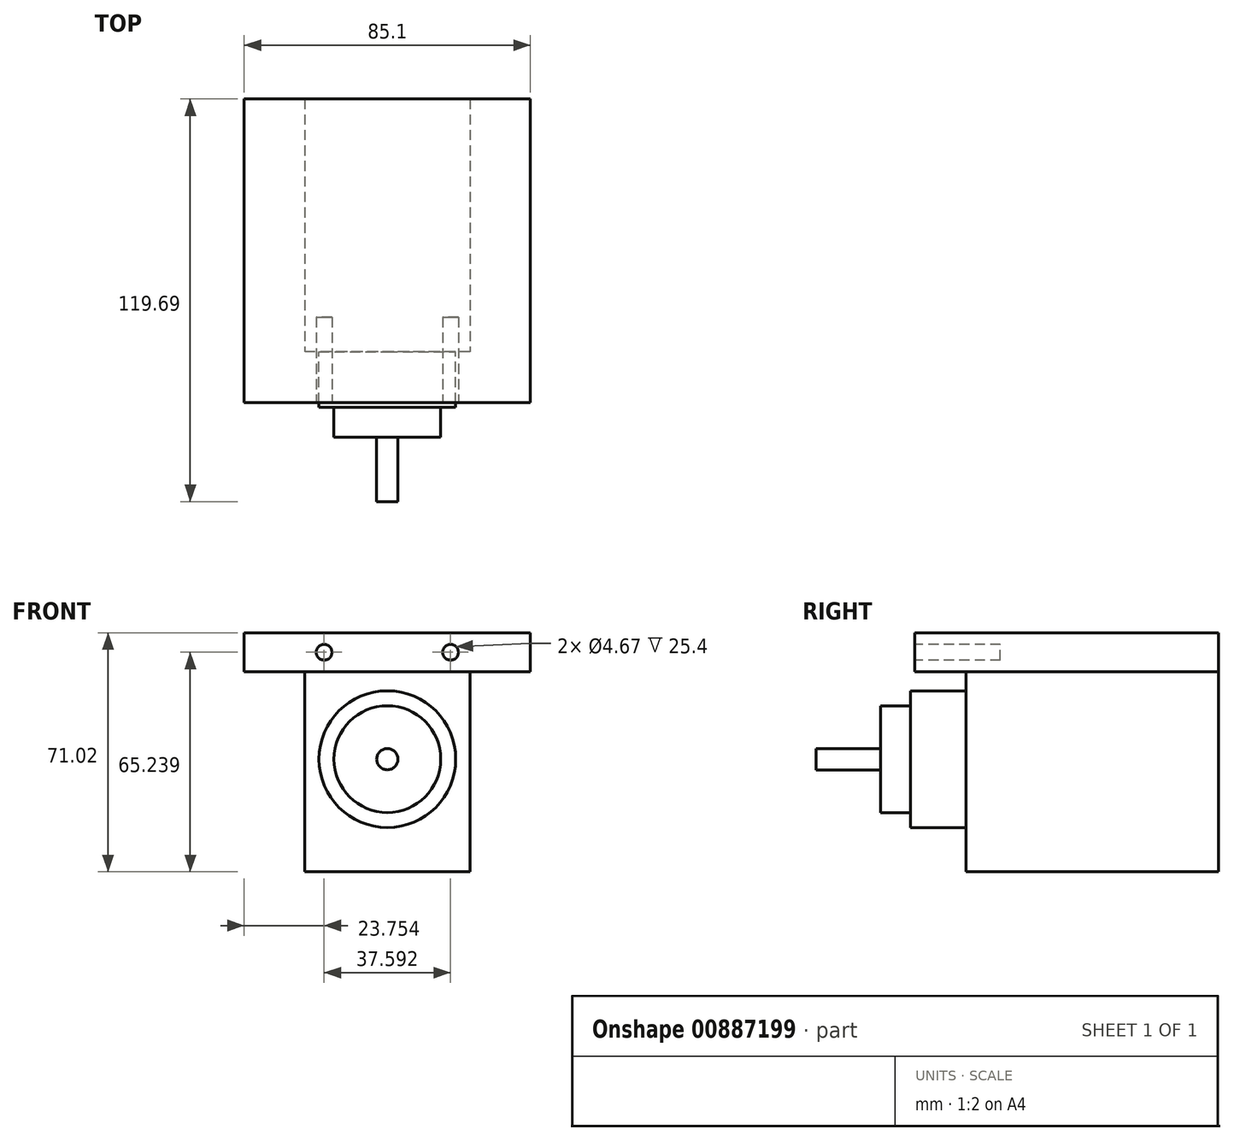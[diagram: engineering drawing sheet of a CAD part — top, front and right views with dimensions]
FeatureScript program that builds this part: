
annotation { "Feature Type Name" : "Feature", "Feature Type Description" : "" }
export const myFeature = defineFeature(function(context is Context, id is Id, definition is map)
    precondition{}
    {
        {
            var Q0;
            Q0=qCreatedBy(makeId("Top.planeOp"),FACE);
            var sketch = newSketch(context, id + "F0", { "sketchPlane" : qUnion([Q0])});
            skLineSegment(sketch, "E0.bottom", {"start": v(42.55, -45.14) * mm, "end": v(-42.55, -45.14) * mm});
            skLineSegment(sketch, "E0.top", {"start": v(42.55, 45.14) * mm, "end": v(-42.55, 45.14) * mm});
            skLineSegment(sketch, "E0.left", {"start": v(42.55, -45.14) * mm, "end": v(42.55, 45.14) * mm});
            skLineSegment(sketch, "E0.right", {"start": v(-42.55, -45.14) * mm, "end": v(-42.55, 45.14) * mm});
            skPoint(sketch, "E0.middle", {"position": v(0, 0) * mm});
            skSolve(sketch);
        }
        {
            var Q0;
            Q0=makeQuery(id+"F0.imprint","IMPRINT",FACE,{"disambiguationData":[TD([[makeQuery(id+"F0.imprint","IMPRINT",EDGE,{"derivedFrom":sQuery(id+"F0.wireOp",EDGE,"E0.bottom")}),-1.0]])]});
            extrude(context, id + "F1", {"entities" : qUnion([Q0]), "depth" : 11.56 * mm, "offsetDistance" : 25.4 * mm});
        }
        {
            var Q0;
            Q0=makeQuery(id+"F1.opExtrude","CAP_FACE",FACE,{"disambiguationData":[OSD([sQuery(id+"F0.wireOp",EDGE,"E0.bottom"),sQuery(id+"F0.wireOp",EDGE,"E0.top"),sQuery(id+"F0.wireOp",EDGE,"E0.left"),sQuery(id+"F0.wireOp",EDGE,"E0.right")])],"isStart":true});
            var sketch = newSketch(context, id + "F2", { "sketchPlane" : qUnion([Q0])});
            skLineSegment(sketch, "E1.bottom", {"start": v(24.53, -29.97) * mm, "end": v(-24.53, -29.97) * mm});
            skLineSegment(sketch, "E1.top", {"start": v(24.53, 29.97) * mm, "end": v(-24.53, 29.97) * mm});
            skLineSegment(sketch, "E1.left", {"start": v(24.53, -29.97) * mm, "end": v(24.53, 29.97) * mm});
            skLineSegment(sketch, "E1.right", {"start": v(-24.53, -29.97) * mm, "end": v(-24.53, 29.97) * mm});
            skPoint(sketch, "E1.middle", {"position": v(0, 0) * mm});
            skSolve(sketch);
        }
        {
            var Q0;
            Q0=makeQuery(id+"F2.imprint","IMPRINT",FACE,{"disambiguationData":[TD([[makeQuery(id+"F2.imprint","IMPRINT",EDGE,{"derivedFrom":sQuery(id+"F2.wireOp",EDGE,"E1.bottom")}),-1.0]])]});
            extrude(context, id + "F3", {"entities" : qUnion([Q0]), "operationType" : NewBodyOperationType.ADD, "depth" : 59.46 * mm, "offsetDistance" : 25.4 * mm});
        }
        {
            var Q0;
            Q0=makeQuery(id+"F3.opExtrude","SWEPT_FACE",FACE,{"disambiguationData":[OSD([sQuery(id+"F2.wireOp",EDGE,"E1.top")])]});
            var sketch = newSketch(context, id + "F4", { "sketchPlane" : qUnion([Q0])});
            skCircle(sketch, "E2", {"center": v(0, -25.98) * mm, "radius": 20.32 * mm});
            skCircle(sketch, "E3", {"center": v(0, -25.98) * mm, "radius": 15.88 * mm});
            skCircle(sketch, "E4", {"center": v(0, -25.98) * mm, "radius": 3.18 * mm});
            skSolve(sketch);
        }
        {
            var Q0;
            Q0=makeQuery(id+"F4.imprint","IMPRINT",FACE,{"disambiguationData":[TD([[makeQuery(id+"F4.imprint","IMPRINT",EDGE,{"derivedFrom":sQuery(id+"F4.wireOp",EDGE,"E2")}),1.0]])]});
            extrude(context, id + "F5", {"entities" : qUnion([Q0]), "operationType" : NewBodyOperationType.ADD, "depth" : 16.5 * mm, "offsetDistance" : 25.4 * mm});
        }
        {
            var Q0;
            Q0=makeQuery(id+"F4.imprint","IMPRINT",FACE,{"disambiguationData":[TD([[makeQuery(id+"F4.imprint","IMPRINT",EDGE,{"derivedFrom":sQuery(id+"F4.wireOp",EDGE,"E3")}),1.0]])]});
            extrude(context, id + "F6", {"entities" : qUnion([Q0]), "operationType" : NewBodyOperationType.ADD, "depth" : 25.4 * mm, "offsetDistance" : 25.4 * mm});
        }
        {
            var Q0;
            Q0=makeQuery(id+"F4.imprint","IMPRINT",FACE,{"disambiguationData":[TD([[makeQuery(id+"F4.imprint","IMPRINT",EDGE,{"derivedFrom":sQuery(id+"F4.wireOp",EDGE,"E4")}),1.0]])]});
            extrude(context, id + "F7", {"entities" : qUnion([Q0]), "operationType" : NewBodyOperationType.ADD, "depth" : 44.58 * mm, "offsetDistance" : 25.4 * mm});
        }
        {
            var Q0;
            Q0=makeQuery(id+"F1.opExtrude","SWEPT_FACE",FACE,{"disambiguationData":[OSD([sQuery(id+"F0.wireOp",EDGE,"E0.bottom")])]});
            var sketch = newSketch(context, id + "F8", { "sketchPlane" : qUnion([Q0])});
            skCircle(sketch, "E5", {"center": v(-18.8, 5.78) * mm, "radius": 2.34 * mm});
            skPoint(sketch, "E5.centerSnap0", {"position": v(-42.55, 5.78) * mm});
            skCircle(sketch, "E6.MirrorC", {"center": v(18.8, 5.78) * mm, "radius": 2.34 * mm});
            skSolve(sketch);
        }
        {
            var Q0;
            Q0 = qSketchRegion(id + "F8", true);
            extrude(context, id + "F9", {"entities" : qUnion([Q0]), "operationType" : NewBodyOperationType.REMOVE, "oppositeDirection" : true, "depth" : 25.4 * mm, "offsetDistance" : 25.4 * mm});
        }
        {
            var Q0;
            Q0=makeQuery(id+"F3.opExtrude","SWEPT_FACE",FACE,{"disambiguationData":[OSD([sQuery(id+"F2.wireOp",EDGE,"E1.bottom")])]});
            var Q1;
            Q1=makeQuery(id+"F1.opExtrude","SWEPT_FACE",FACE,{"disambiguationData":[OSD([sQuery(id+"F0.wireOp",EDGE,"E0.top")])]});
            extrude(context, id + "F10", {"entities" : qUnion([Q0]), "operationType" : NewBodyOperationType.ADD, "endBound" : BoundingType.UP_TO_SURFACE, "depth" : 25.4 * mm, "endBoundEntityFace" : qUnion([Q1]), "offsetDistance" : 25.4 * mm});
        }
    });
